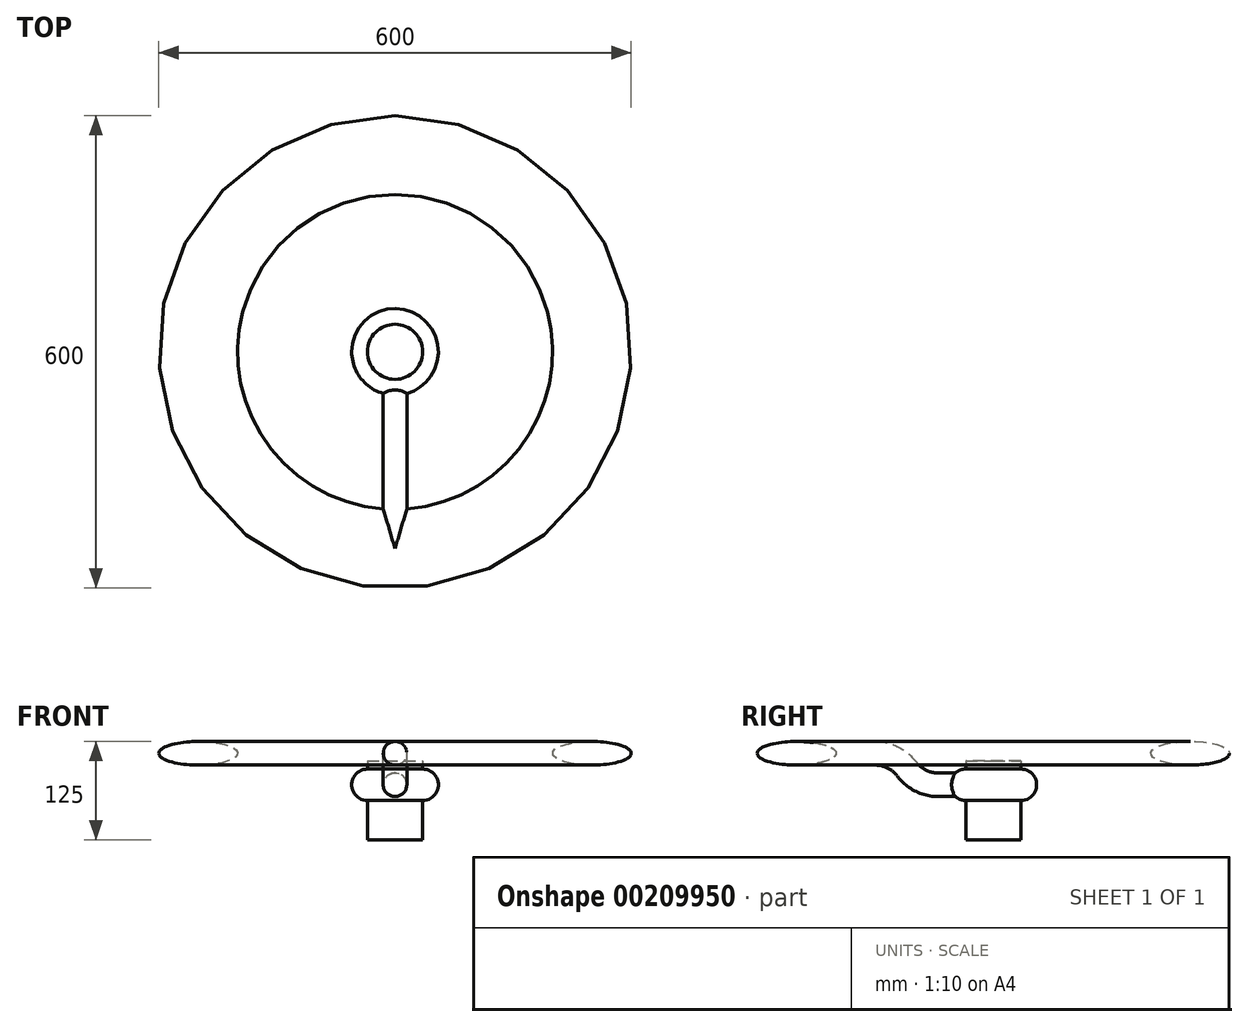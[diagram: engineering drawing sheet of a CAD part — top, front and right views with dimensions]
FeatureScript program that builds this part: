
annotation { "Feature Type Name" : "Feature", "Feature Type Description" : "" }
export const myFeature = defineFeature(function(context is Context, id is Id, definition is map)
    precondition{}
    {
        {
            var Q0;
            Q0=qCreatedBy(makeId("Front.planeOp"),FACE);
            var sketch = newSketch(context, id + "F0", { "sketchPlane" : qUnion([Q0])});
            skLineSegment(sketch, "E0", {"start": v(0, 0) * mm, "end": v(0, 100) * mm});
            skLineSegment(sketch, "E1", {"start": v(0, 100) * mm, "end": v(-35, 100) * mm});
            skLineSegment(sketch, "E2", {"start": v(-35, 100) * mm, "end": v(-35, 90) * mm});
            skLineSegment(sketch, "E3", {"start": v(-35, 0) * mm, "end": v(0, 0) * mm});
            skArc(sketch, "E4", {"start": v(-35, 90) * mm, "mid": v(-55, 70) * mm, "end": v(-35, 50) * mm});
            skLineSegment(sketch, "E5.trimOffspring", {"start": v(-35, 50) * mm, "end": v(-35, 0) * mm});
            skSolve(sketch);
        }
        {
            var Q0;
            Q0=makeQuery(id+"F0.imprint","IMPRINT",FACE,{"disambiguationData":[TD([[makeQuery(id+"F0.imprint","IMPRINT",EDGE,{"derivedFrom":sQuery(id+"F0.wireOp",EDGE,"E0")}),1.0]])]});
            var Q1;
            Q1=sQuery(id+"F0.wireOp",EDGE,"E0");
            revolve(context, id + "F1", {"entities" : qUnion([Q0]), "axis" : qUnion([Q1]), "revolveType" : RevolveType.FULL});
        }
        {
            var Q0;
            Q0=qCreatedBy(makeId("Right.planeOp"),FACE);
            var sketch = newSketch(context, id + "F2", { "sketchPlane" : qUnion([Q0])});
            skEllipse(sketch, "E6", {"center": v(-250, 110) * mm, "majorRadius": 50 * mm, "minorRadius": 15 * mm, "majorAxis": v(1, 0)});
            skLineSegment(sketch, "E7", {"start": v(0, 0) * mm, "end": v(0, 136) * mm});
            skSolve(sketch);
        }
        {
            var Q0;
            Q0 = qSketchRegion(id + "F2", true);
            var Q1;
            Q1=sQuery(id+"F2.wireOp",EDGE,"E7");
            revolve(context, id + "F3", {"entities" : qUnion([Q0]), "axis" : qUnion([Q1]), "revolveType" : RevolveType.FULL});
        }
        {
            var Q0;
            Q0=qCreatedBy(makeId("Right.planeOp"),FACE);
            var sketch = newSketch(context, id + "F4", { "sketchPlane" : qUnion([Q0])});
            skLineSegment(sketch, "E8", {"start": v(-250, 110) * mm, "end": v(-150, 110) * mm});
            skArc(sketch, "E9", {"start": v(-150, 110) * mm, "mid": v(-127.64, 104.72) * mm, "end": v(-110, 90) * mm});
            skArc(sketch, "E10", {"start": v(-110, 90) * mm, "mid": v(-92.36, 75.28) * mm, "end": v(-70, 70) * mm});
            skLineSegment(sketch, "E11", {"start": v(-70, 70) * mm, "end": v(0, 70) * mm});
            skSolve(sketch);
        }
        {
            var Q0;
            Q0=qCreatedBy(makeId("Front.planeOp"),FACE);
            var sketch = newSketch(context, id + "F5", { "sketchPlane" : qUnion([Q0])});
            skCircle(sketch, "E12", {"center": v(0, 70) * mm, "radius": 15 * mm});
            skSolve(sketch);
        }
        {
            var Q0;
            Q0 = qSketchRegion(id + "F5", true);
            var Q1;
            Q1 = qConstructionFilter(qBodyType(qCreatedBy(id + "F4" ,EDGE), BodyType.WIRE), ConstructionObject.NO);
            sweep(context, id + "F6", {"operationType" : NewBodyOperationType.ADD, "profiles" : qUnion([Q0]), "path" : qUnion([Q1])});
        }
    });
